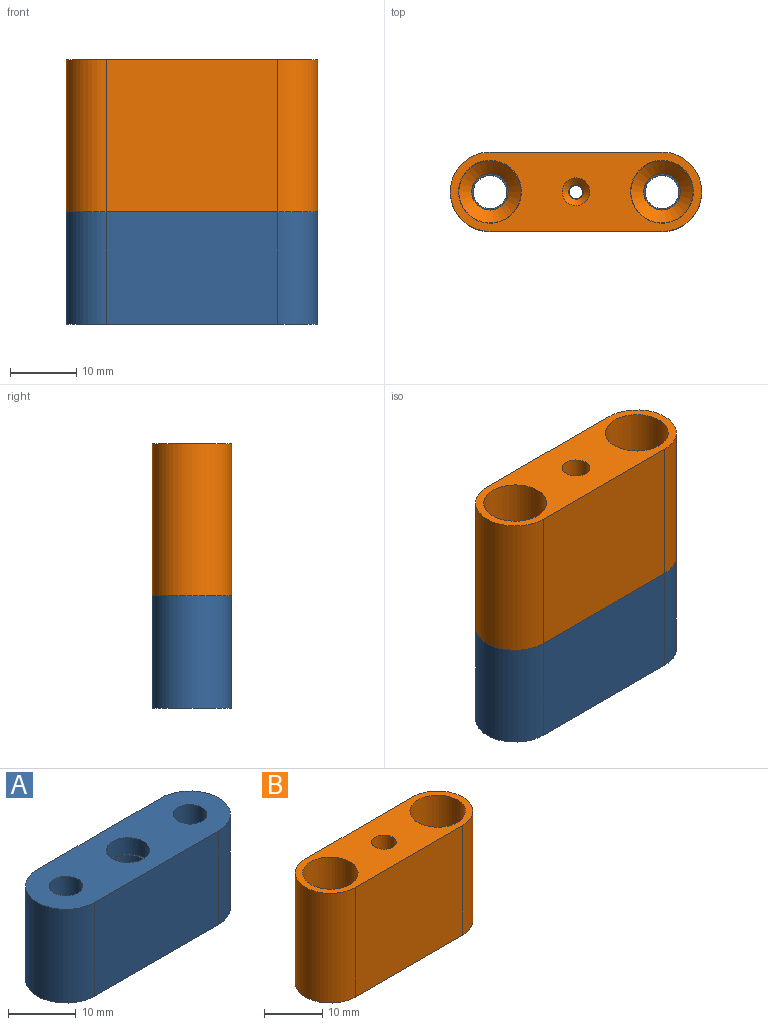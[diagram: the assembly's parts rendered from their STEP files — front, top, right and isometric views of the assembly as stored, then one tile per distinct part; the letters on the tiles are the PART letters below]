
ASSEMBLY  parts=2 mates=1
PART A: 19 faces, bbox 38x12x17 mm
  f0: cylinder r=6mm len=17mm, axis (0,0,1), area 0.5mm2, adj f7,f8,f10,f16
  f1: cylinder r=1mm len=2mm, axis (0,0,1), area 5mm2, adj f2,f18
  f2: cone r=2mm half-angle=39.8deg, axis (0,0,1), area 14.7mm2, adj f1,f3
  f3: plane 6x6mm, normal (0,0,1), area 15.7mm2, adj f2,f4
  f4: cylinder r=3mm len=6mm, axis (0,0,1), area 113.1mm2, adj f3,f5
  f5: plane 6.4x6.4mm, normal (0,0,1), area 3.9mm2, adj f4,f6
  f6: cylinder r=3.2mm len=6.4mm, axis (0,0,1), area 60.3mm2, adj f5,f7
  f7: plane 38x12mm, normal (0,0,1), area 353.7mm2, adj f0,f6,f10,f11,f12,f13,f14,f15
  f8: plane 38x12mm, normal (0,0,-1), area 357.6mm2, adj f0,f10,f11,f12,f13,f14,f15,f16
  f9: cylinder r=2mm len=4mm, axis (0,0,1), area 50.3mm2, adj f17,f18
  f10: plane 17x12.97mm, normal (0,1,0), area 220.5mm2, adj f0,f7,f8,f11
  f11: cylinder r=6mm len=17mm, axis (0,0,1), area 320.7mm2, adj f7,f8,f10,f13
  f12: cylinder r=2.5mm len=17mm, axis (0,0,1), area 267mm2, adj f7,f8
  f13: plane 26x17mm, normal (0,-1,0), area 442mm2, adj f7,f8,f11,f14
  f14: cylinder r=6mm len=17mm, axis (0,0,1), area 320.7mm2, adj f7,f8,f13,f16
  f15: cylinder r=2.5mm len=17mm, axis (0,0,1), area 267mm2, adj f7,f8
  f16: plane 17x12.97mm, normal (0,1,0), area 220.5mm2, adj f0,f7,f8,f14
  f17: cone r=3mm half-angle=45deg, axis (0,0,-1), area 22.2mm2, adj f8,f9
  f18: cone r=2mm half-angle=45deg, axis (0,0,-1), area 13.3mm2, adj f1,f9
PART B: 26 faces, bbox 38x12x26 mm
  f0: cylinder r=6mm len=23mm, axis (0,0,-1), area 0.7mm2, adj f7,f8,f15,f16
  f1: cylinder r=2.2mm len=13mm, axis (0,0,-1), area 179.7mm2, adj f2,f11
  f2: plane 6x6mm, normal (0,0,-1), area 13.1mm2, adj f1,f3
  f3: cylinder r=3mm len=6mm, axis (0,0,-1), area 75.4mm2, adj f2,f4
  f4: cone r=3.95mm half-angle=49.9deg, axis (0,0,1), area 27.1mm2, adj f3,f5
  f5: cone r=4.9mm half-angle=49.9deg, axis (0,0,-1), area 34.5mm2, adj f4,f6
  f6: cylinder r=4.9mm len=9.8mm, axis (0,0,-1), area 30.8mm2, adj f5,f7
  f7: plane 38x12mm, normal (0,0,-1), area 302.2mm2, adj f0,f6,f12,f13,f14,f15,f16,f24
  f8: plane 38x12mm, normal (0,0,1), area 269.5mm2, adj f0,f9,f12,f13,f14,f15,f16,f17
  f9: cylinder r=2.1mm len=8mm, axis (0,0,-1), area 105.6mm2, adj f8,f23
  f10: cylinder r=1.1mm len=4mm, axis (0,0,-1), area 27.6mm2, adj f11,f23
  f11: plane 4.4x4.4mm, normal (0,0,-1), area 11.4mm2, adj f1,f10
  f12: plane 26x23mm, normal (0,-1,0), area 598mm2, adj f7,f8,f13,f14
  f13: cylinder r=6mm len=23mm, axis (0,0,-1), area 433.9mm2, adj f7,f8,f12,f16
  f14: cylinder r=6mm len=23mm, axis (0,0,-1), area 433.9mm2, adj f7,f8,f12,f15
  f15: plane 23x12.97mm, normal (0,1,0), area 298.3mm2, adj f0,f7,f8,f14
  f16: plane 23x12.97mm, normal (0,1,0), area 298.3mm2, adj f0,f7,f8,f13
  f17: cylinder r=4.75mm len=9.5mm, axis (0,0,1), area 208.9mm2, adj f8,f18
  f18: plane 9.5x9.5mm, normal (0,0,1), area 1.5mm2, adj f17,f21
  f19: plane 9.5x9.5mm, normal (0,0,1), area 1.5mm2, adj f20,f22
  f20: cylinder r=4.75mm len=9.5mm, axis (0,0,1), area 208.9mm2, adj f8,f19
  f21: cone r=2.5mm half-angle=45deg, axis (0,0,1), area 64.5mm2, adj f18,f25
  f22: cone r=4.7mm half-angle=45deg, axis (0,0,1), area 64.5mm2, adj f19,f24
  f23: cone r=2.1mm half-angle=45deg, axis (0,0,1), area 14.2mm2, adj f9,f10
  f24: cylinder r=2.75mm len=14.05mm, axis (0,0,-1), area 242.8mm2, adj f7,f22
  f25: cylinder r=2.75mm len=14.05mm, axis (0,0,-1), area 242.8mm2, adj f7,f21
PLACE A t=(-0.22,0.55,1.14)mm
PLACE B t=(12.78,0.55,10.14)mm
MATE fastened B.f0 <-> A.f0  axis (0,0,-1) through (-0.22,0.55,10.14)mm
